# Revit family: OLI_TREND_215x145x2
name_source: partatom
category: Plumbing Fixtures
revit_build: Autodesk Revit Architecture 2016 (Build: 20150220_1215(x64)
units: mm (PartAtom-declared; Revit-internal decimal feet)

## family parameters
Always vertical = Yes
Cut with Voids When Loaded = No
OmniClass Number = 23.45.00.00
OmniClass Title = Sanitary, Laundry, and Cleaning Equipment
Part Type = Normal
Room Calculation Point = No
Round Connector Dimension = Use Diameter
Shared = No
Work Plane-Based = Yes

## types (2) — shared parameters
BIM object developer = www.concepsysbim.com
CONTROL_Actuation type = Pneumatic
CONTROL_Brand = OLI
CONTROL_Brief description = Dictating the rules of style
CONTROL_Height = 145 mm  [stored 0.475722 ft]
CONTROL_Installation instructions = http://www.oli-world.com
CONTROL_Length = 215 mm  [stored 0.705381 ft]
CONTROL_Material = Stainless steel
CONTROL_Model = Trend
CONTROL_Product data url = http://www.oli-world.com
CONTROL_Technical description = http://www.oli-world.com
CONTROL_Type of flush = Dual Flush
CONTROL_Type/function = control plate for concealed cisterns
CONTROL_Vandal-proof = yes
CONTROL_Website/webpage = http://www.oli-world.com
CONTROL_Width = 2 mm  [stored 0.00656168 ft]
Default Elevation = 1219.2 mm  [stored 4 ft]
Description = Dictating the rules of style
Fax = (+351) 234 300 210
HORIZONTAL = No
Manufacturer = OLI
Model = Trend
Product data url = http://bimobject.com
Revision = 2.0PT
Telefone = (+351) 234 300 200
URL = http://www.oli-world.com
VERTICAL = Yes

## per-type parameters (varying)
| type | CONTROL_Model Series | CONTROL_Model code/ref |
| OLI_Pneumatic_Polished stainless steel | Polished stainless steel | CG24000639914 |
| OLI_Pneumatic_Brushed Stainless Steel | Brushed stainless steel | CG24000639916 |

note: [stored X ft] marks values corroborated as IEEE doubles in the binary element streams (Revit-internal decimal feet)

## geometry (parser evidence)
native form markers: Sweep x6
no freeform markers — native parametric forms only
